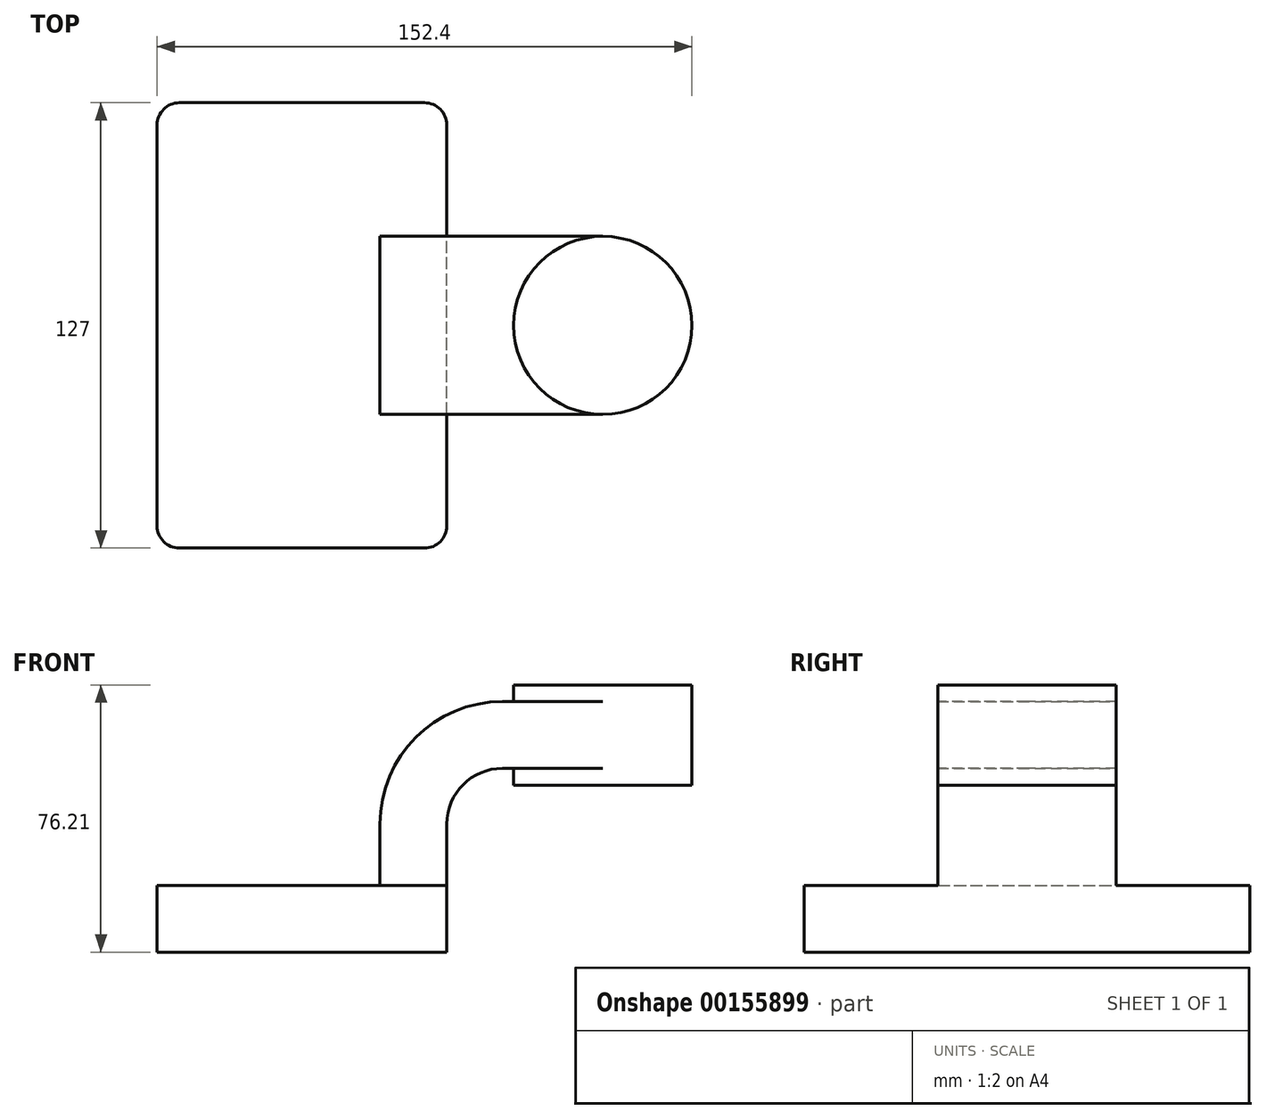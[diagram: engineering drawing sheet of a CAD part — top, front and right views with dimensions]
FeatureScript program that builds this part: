
annotation { "Feature Type Name" : "Feature", "Feature Type Description" : "" }
export const myFeature = defineFeature(function(context is Context, id is Id, definition is map)
    precondition{}
    {
        {
            var Q0;
            Q0=qCreatedBy(makeId("Front.planeOp"),FACE);
            var sketch = newSketch(context, id + "F0", { "sketchPlane" : qUnion([Q0])});
            skLineSegment(sketch, "E0.bottom", {"start": v(41.27, 9.53) * mm, "end": v(-41.28, 9.53) * mm});
            skLineSegment(sketch, "E0.top", {"start": v(41.28, -9.52) * mm, "end": v(-41.27, -9.52) * mm});
            skLineSegment(sketch, "E0.left", {"start": v(41.28, 9.53) * mm, "end": v(41.28, -9.52) * mm});
            skLineSegment(sketch, "E0.right", {"start": v(-41.28, 9.53) * mm, "end": v(-41.27, -9.52) * mm});
            skPoint(sketch, "E0.middle", {"position": v(0, 0) * mm});
            skLineSegment(sketch, "E1.bottom", {"start": v(111.12, 66.68) * mm, "end": v(60.32, 66.68) * mm});
            skLineSegment(sketch, "E1.top", {"start": v(111.12, 38.1) * mm, "end": v(60.32, 38.1) * mm});
            skLineSegment(sketch, "E1.left", {"start": v(111.12, 66.68) * mm, "end": v(111.12, 38.1) * mm});
            skLineSegment(sketch, "E1.right", {"start": v(60.32, 66.68) * mm, "end": v(60.32, 38.1) * mm});
            skPoint(sketch, "E1.middle", {"position": v(85.72, 52.39) * mm});
            skLineSegment(sketch, "E2", {"start": v(41.27, 9.53) * mm, "end": v(41.27, 27) * mm});
            skArc(sketch, "E3", {"start": v(41.27, 27) * mm, "mid": v(45.92, 38.23) * mm, "end": v(57.15, 42.88) * mm});
            skLineSegment(sketch, "E4", {"start": v(57.15, 42.88) * mm, "end": v(85.72, 42.88) * mm});
            skLineSegment(sketch, "E5.0", {"start": v(57.15, 61.93) * mm, "end": v(85.72, 61.93) * mm});
            skArc(sketch, "E5.1", {"start": v(22.23, 27) * mm, "mid": v(32.45, 51.7) * mm, "end": v(57.15, 61.93) * mm});
            skLineSegment(sketch, "E5.2", {"start": v(22.22, 9.53) * mm, "end": v(22.22, 27) * mm});
            skLineSegment(sketch, "E6", {"start": v(85.72, 38.1) * mm, "end": v(85.72, 66.68) * mm});
            skPoint(sketch, "E7.orphan", {"position": v(96.13, 42.88) * mm});
            skFitSpline(sketch, "E8", {"points": [v(-41.28, 9.52) * mm, v(57.15, 61.93) * mm], "startDerivative": vector(44.89, 78.07) * mm, "endDerivative": vector(143.41, -3.92) * mm});
            skSolve(sketch);
        }
        {
            var Q0;
            Q0=makeQuery(id+"F0.imprint","IMPRINT",FACE,{"disambiguationData":[TD([[makeQuery(id+"F0.imprint","IMPRINT",EDGE,{"derivedFrom":sQuery(id+"F0.wireOp",EDGE,"E0.top")}),-1.0]])]});
            extrude(context, id + "F1", {"entities" : qUnion([Q0]), "endBound" : BoundingType.SYMMETRIC, "depth" : 127 * mm});
        }
        {
            var Q0;
            {var subQ2=sQuery(id+"F0.wireOp",EDGE,"E2");Q0=makeQuery(id+"F0.imprint","IMPRINT",FACE,{"disambiguationData":[TD([[makeQuery(id+"F0.imprint","IMPRINT",EDGE,{"derivedFrom":subQ2}),1.0]])]});}
            var Q1;
            {var subQ0=sQuery(id+"F0.wireOp",EDGE,"E5.0");var subQ1=sQuery(id+"F0.wireOp",EDGE,"E1.right");var subQ2=makeQuery(id+"F0.imprint","INTERSECT",VERTEX,{"derivedFrom":[subQ1,subQ0]});Q1=makeQuery(id+"F0.imprint","IMPRINT",FACE,{"disambiguationData":[TD([[makeQuery(id+"F0.imprint","IMPRINT",EDGE,{"disambiguationData":[TD([[subQ2,-1.0]])],"derivedFrom":subQ1}),1.0]])]});}
            extrude(context, id + "F2", {"entities" : qUnion([Q0, Q1]), "operationType" : NewBodyOperationType.ADD, "endBound" : BoundingType.SYMMETRIC, "depth" : 50.8 * mm});
        }
        {
            var Q0;
            Q0=makeQuery(id+"F0.imprint","IMPRINT",FACE,{"disambiguationData":[TD([[makeQuery(id+"F0.imprint","IMPRINT",EDGE,{"derivedFrom":sQuery(id+"F0.wireOp",EDGE,"E5.1")}),1.0]])]});
            extrude(context, id + "F3", {"entities" : qUnion([Q0]), "operationType" : NewBodyOperationType.ADD, "endBound" : BoundingType.SYMMETRIC, "depth" : 15.88 * mm});
        }
        {
            var Q0;
            {var subQ4=sQuery(id+"F0.wireOp",EDGE,"E1.left");Q0=makeQuery(id+"F0.imprint","IMPRINT",FACE,{"disambiguationData":[TD([[makeQuery(id+"F0.imprint","IMPRINT",EDGE,{"derivedFrom":subQ4}),-1.0]])]});}
            var Q1;
            Q1=sQuery(id+"F0.wireOp",EDGE,"E6");
            revolve(context, id + "F4", {"operationType" : NewBodyOperationType.ADD, "entities" : qUnion([Q0]), "axis" : qUnion([Q1]), "revolveType" : RevolveType.FULL});
        }
        {
            var Q0;
            Q0=makeQuery(id+"F1.opExtrude","CAP_EDGE",EDGE,{"disambiguationData":[OSD([sQuery(id+"F0.wireOp",EDGE,"E0.left")])],"isStart":false});
            var Q1;
            Q1=makeQuery(id+"F1.opExtrude","CAP_EDGE",EDGE,{"disambiguationData":[OSD([sQuery(id+"F0.wireOp",EDGE,"E0.right")])],"isStart":false});
            var Q2;
            Q2=makeQuery(id+"F1.opExtrude","CAP_EDGE",EDGE,{"disambiguationData":[OSD([sQuery(id+"F0.wireOp",EDGE,"E0.left")])],"isStart":true});
            var Q3;
            Q3=makeQuery(id+"F1.opExtrude","CAP_EDGE",EDGE,{"disambiguationData":[OSD([sQuery(id+"F0.wireOp",EDGE,"E0.right")])],"isStart":true});
            fillet(context, id + "F5", {"entities" : qUnion([Q0, Q1, Q2, Q3]), "radius" : 6.35 * mm, "tangentPropagation" : true, "allowEdgeOverflow" : false});
        }
    });
